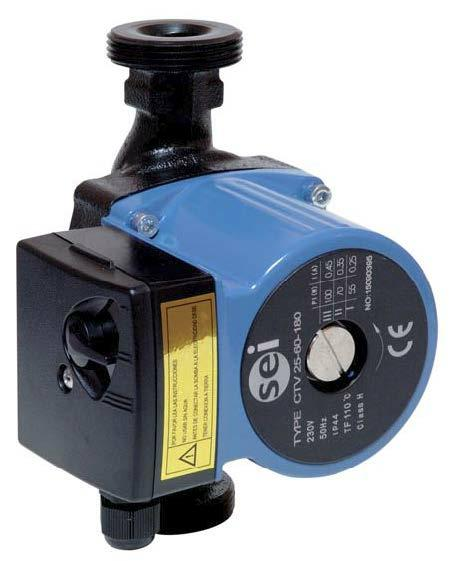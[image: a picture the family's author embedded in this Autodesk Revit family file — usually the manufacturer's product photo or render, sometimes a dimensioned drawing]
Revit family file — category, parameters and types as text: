
# Revit family: CTV_25-60-AC52122
name_source: partatom
category: Aparatos eléctricos
revit_build: Autodesk Revit 2016 (Build: 20150220_1215(x64)
units: mm (PartAtom-declared; Revit-internal decimal feet)

## family parameters
Compartido = No
Corte con vacíos al cargar = No
Cota de conector redondo = Diámetro de uso
Mantener orientación de anotación = No
Número OmniClass = 23.80.00.00
Punto de cálculo de habitación = No
Se basa en plano de trabajo = No
Siempre vertical = Sí
Tipo de pieza = Caja de conexiones
Título OmniClass = Electric Power and Lighting

## types (2) — shared parameters
Fabricante = SALVADOR ESCODA
URL = www.salvadorescoda.com
zero-valued in all types: Costo

## per-type parameters (varying)
| type | Aislamiento | Caudal | Conexión rácores | Código de montaje | Descripción | Dimensiones Unidad Interior | Imagen de tipo | Intensidad máx. | Modelo | Motor | Máx. presión trabajo | Peso | Potencia máx | Presión disponible | Protección | Rango temperatura agua | Regulable | Temperatura ambiente |
| MVD-22T2 | 35 dB(A) |  |  | CL23370 | CONDUCTO BAJA SILUETA | 700 x 210 x 500 mm | <Ninguno> |  | MVD-22T2/DHN1-DA5 | 521 m3/h | 2,2kW / 39W | 17,5 kg neto |  |  | 6,35 mm (1/4") | 2,6kW / 39W |  | DC / WZDK100-38GS |
| CTV | Clase H | 1,8 m3/h | 1 1/2" DN | AC52122 | BOMBA CIRCULADORA PARA CALEFACCION | 180 x 130 x 130 mm | SEI_CTV.jpg | 0,45 A | CTV 25-65 | 2 polos, 1x230V - 50Hz | 10 bar | 3,34 Kgs | 100 W | 4 m.c.a. | IP 44 | 2º a 110 ºC | 3 velocidades | Hasta 40ºC |
